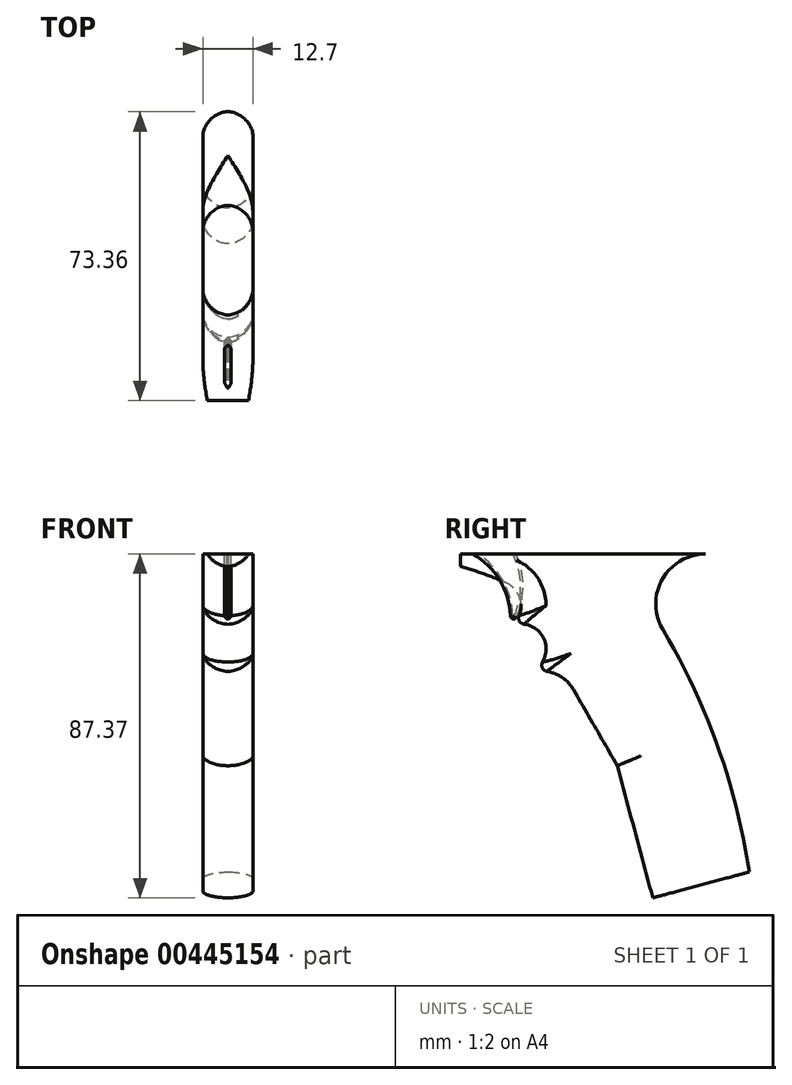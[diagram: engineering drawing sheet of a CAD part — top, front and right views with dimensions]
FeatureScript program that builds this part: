
annotation { "Feature Type Name" : "Feature", "Feature Type Description" : "" }
export const myFeature = defineFeature(function(context is Context, id is Id, definition is map)
    precondition{}
    {
        {
            var Q0;
            Q0=qCreatedBy(makeId("Right.planeOp"),FACE);
            var sketch = newSketch(context, id + "F0", { "sketchPlane" : qUnion([Q0])});
            skLineSegment(sketch, "E0", {"start": v(0, 0) * mm, "end": v(-76.2, 0) * mm});
            skLineSegment(sketch, "E1", {"start": v(-76.2, 0) * mm, "end": v(-76.2, -3.18) * mm});
            skLineSegment(sketch, "E2", {"start": v(-38.1, 0) * mm, "end": v(-12.7, -44) * mm});
            skLineSegment(sketch, "E3", {"start": v(-12.7, -44) * mm, "end": v(-2.84, -80.8) * mm});
            skLineSegment(sketch, "E4", {"start": v(-2.84, -80.8) * mm, "end": v(-27.37, -87.37) * mm});
            skLineSegment(sketch, "E5", {"start": v(-12.7, -44) * mm, "end": v(-36.37, -53.8) * mm});
            skLineSegment(sketch, "E6", {"start": v(-27.37, -87.37) * mm, "end": v(-36.37, -53.8) * mm});
            skLineSegment(sketch, "E7", {"start": v(-36.37, -53.8) * mm, "end": v(-67.43, 0) * mm});
            skArc(sketch, "E8", {"start": v(-2.84, -80.8) * mm, "mid": v(-10.85, -48.93) * mm, "end": v(-24.84, -19.19) * mm});
            skArc(sketch, "E9", {"start": v(-13.92, 0) * mm, "mid": v(-24.96, -6.42) * mm, "end": v(-24.84, -19.19) * mm});
            skArc(sketch, "E10", {"start": v(-64.57, -7.37) * mm, "mid": v(-70.3, -5.05) * mm, "end": v(-76.2, -3.17) * mm});
            skArc(sketch, "E11", {"start": v(-55.37, -27.43) * mm, "mid": v(-55.1, -21.37) * mm, "end": v(-60.05, -17.86) * mm});
            skArc(sketch, "E12", {"start": v(-61.32, -15.66) * mm, "mid": v(-61.25, -10.85) * mm, "end": v(-64.57, -7.37) * mm});
            skArc(sketch, "E13", {"start": v(-47.53, -34.46) * mm, "mid": v(-50.37, -31.38) * mm, "end": v(-54.26, -29.82) * mm});
            skArc(sketch, "E14", {"start": v(-55.37, -27.43) * mm, "mid": v(-55.45, -28.92) * mm, "end": v(-54.26, -29.82) * mm});
            skArc(sketch, "E15", {"start": v(-61.32, -15.66) * mm, "mid": v(-61.24, -17.08) * mm, "end": v(-60.05, -17.86) * mm});
            skPoint(sketch, "E16.orphan", {"position": v(-62.67, -8.25) * mm});
            skSolve(sketch);
        }
        {
            var Q0;
            {var subQ3=sQuery(id+"F0.wireOp",EDGE,"E2");Q0=makeQuery(id+"F0.imprint","IMPRINT",FACE,{"disambiguationData":[TD([[makeQuery(id+"F0.imprint","IMPRINT",EDGE,{"derivedFrom":subQ3}),-1.0]])]});}
            var Q1;
            {var subQ0=sQuery(id+"F0.wireOp",EDGE,"E2");Q1=makeQuery(id+"F0.imprint","IMPRINT",FACE,{"disambiguationData":[TD([[makeQuery(id+"F0.imprint","IMPRINT",EDGE,{"derivedFrom":subQ0}),1.0]])]});}
            var Q2;
            Q2=makeQuery(id+"F0.imprint","IMPRINT",FACE,{"disambiguationData":[TD([[makeQuery(id+"F0.imprint","IMPRINT",EDGE,{"derivedFrom":sQuery(id+"F0.wireOp",EDGE,"E3")}),-1.0]])]});
            var Q3;
            {var subQ0=sQuery(id+"F0.wireOp",EDGE,"E3");Q3=makeQuery(id+"F0.imprint","IMPRINT",FACE,{"disambiguationData":[TD([[makeQuery(id+"F0.imprint","IMPRINT",EDGE,{"derivedFrom":subQ0}),1.0]])]});}
            var Q4;
            {var subQ4=sQuery(id+"F0.wireOp",EDGE,"E6");Q4=makeQuery(id+"F0.imprint","IMPRINT",FACE,{"disambiguationData":[TD([[makeQuery(id+"F0.imprint","IMPRINT",EDGE,{"derivedFrom":subQ4}),1.0]])]});}
            var Q5;
            {var subQ5=sQuery(id+"F0.wireOp",EDGE,"E14");Q5=makeQuery(id+"F0.imprint","IMPRINT",FACE,{"disambiguationData":[TD([[makeQuery(id+"F0.imprint","IMPRINT",EDGE,{"derivedFrom":subQ5}),1.0]])]});}
            var Q6;
            {var subQ5=sQuery(id+"F0.wireOp",EDGE,"E15");Q6=makeQuery(id+"F0.imprint","IMPRINT",FACE,{"disambiguationData":[TD([[makeQuery(id+"F0.imprint","IMPRINT",EDGE,{"derivedFrom":subQ5}),1.0]])]});}
            var Q7;
            {var subQ1=sQuery(id+"F0.wireOp",EDGE,"E1");Q7=makeQuery(id+"F0.imprint","IMPRINT",FACE,{"disambiguationData":[TD([[makeQuery(id+"F0.imprint","IMPRINT",EDGE,{"derivedFrom":subQ1}),1.0]])]});}
            extrude(context, id + "F1", {"entities" : qUnion([Q0, Q1, Q2, Q3, Q4, Q5, Q6, Q7]), "endBound" : BoundingType.SYMMETRIC, "depth" : 12.7 * mm});
        }
        {
            var Q0;
            Q0=makeQuery(id+"F1.opExtrude","CAP_EDGE",EDGE,{"disambiguationData":[OSD([sQuery(id+"F0.wireOp",EDGE,"E13")])],"isStart":true});
            var Q1;
            Q1=makeQuery(id+"F1.opExtrude","CAP_EDGE",EDGE,{"disambiguationData":[OSD([sQuery(id+"F0.wireOp",EDGE,"E11")])],"isStart":false});
            var Q2;
            Q2=makeQuery(id+"F1.opExtrude","CAP_EDGE",EDGE,{"disambiguationData":[OSD([sQuery(id+"F0.wireOp",EDGE,"E7")])],"isStart":false});
            var Q3;
            Q3=makeQuery(id+"F1.opExtrude","CAP_EDGE",EDGE,{"disambiguationData":[OSD([sQuery(id+"F0.wireOp",EDGE,"E7")])],"isStart":true});
            var Q4;
            Q4=makeQuery(id+"F1.opExtrude","CAP_EDGE",EDGE,{"disambiguationData":[OSD([sQuery(id+"F0.wireOp",EDGE,"E6")])],"isStart":false});
            var Q5;
            Q5=makeQuery(id+"F1.opExtrude","CAP_EDGE",EDGE,{"disambiguationData":[OSD([sQuery(id+"F0.wireOp",EDGE,"E6")])],"isStart":true});
            var Q6;
            Q6=makeQuery(id+"F1.opExtrude","CAP_EDGE",EDGE,{"disambiguationData":[OSD([sQuery(id+"F0.wireOp",EDGE,"E8")])],"isStart":true});
            var Q7;
            Q7=makeQuery(id+"F1.opExtrude","CAP_EDGE",EDGE,{"disambiguationData":[OSD([sQuery(id+"F0.wireOp",EDGE,"E8")])],"isStart":false});
            fillet(context, id + "F2", {"entities" : qUnion([Q0, Q1, Q2, Q3, Q4, Q5, Q6, Q7]), "radius" : 6.35 * mm, "tangentPropagation" : true, "rho" : .375, "crossSection" : FilletCrossSection.CONIC, "allowEdgeOverflow" : false});
        }
        {
            var Q0;
            Q0=qCreatedBy(makeId("Right.planeOp"),FACE);
            var sketch = newSketch(context, id + "F3", { "sketchPlane" : qUnion([Q0])});
            skPoint(sketch, "E17.0", {"position": v(-76.2, 0) * mm});
            skLineSegment(sketch, "E18", {"start": v(-76.2, 0) * mm, "end": v(-73.03, 0) * mm});
            skArc(sketch, "E19", {"start": v(-63.51, -15.76) * mm, "mid": v(-66.24, -6.65) * mm, "end": v(-73.03, 0) * mm});
            skLineSegment(sketch, "E20", {"start": v(-76.2, 0) * mm, "end": v(-76.2, -16.5) * mm});
            skLineSegment(sketch, "E21", {"start": v(-76.2, -16.5) * mm, "end": v(-82.55, -16.5) * mm});
            skArc(sketch, "E22", {"start": v(-62, -16.05) * mm, "mid": v(-60.33, -8) * mm, "end": v(-62.2, 0) * mm});
            skLineSegment(sketch, "E23", {"start": v(-73.03, 0) * mm, "end": v(-62.2, 0) * mm});
            skArc(sketch, "E24", {"start": v(-63.51, -15.76) * mm, "mid": v(-62.87, -16.5) * mm, "end": v(-62, -16.05) * mm});
            skLineSegment(sketch, "E25", {"start": v(-79.38, -16.5) * mm, "end": v(-79.38, -8.25) * mm});
            skLineSegment(sketch, "E26", {"start": v(-76.2, -8.25) * mm, "end": v(-79.38, -8.25) * mm});
            skSolve(sketch);
        }
        {
            var Q0;
            Q0=makeQuery(id+"F3.imprint","IMPRINT",FACE,{"disambiguationData":[TD([[makeQuery(id+"F3.imprint","IMPRINT",EDGE,{"derivedFrom":sQuery(id+"F3.wireOp",EDGE,"E19")}),-1.0]])]});
            extrude(context, id + "F4", {"entities" : qUnion([Q0]), "endBound" : BoundingType.SYMMETRIC, "depth" : 1.59 * mm});
        }
        {
            var Q0;
            Q0=makeQuery(id+"F4.opExtrude","CAP_EDGE",EDGE,{"disambiguationData":[OSD([sQuery(id+"F3.wireOp",EDGE,"E19")])],"isStart":false});
            var Q1;
            Q1=makeQuery(id+"F4.opExtrude","CAP_EDGE",EDGE,{"disambiguationData":[OSD([sQuery(id+"F3.wireOp",EDGE,"E24")])],"isStart":false});
            var Q2;
            Q2=makeQuery(id+"F4.opExtrude","CAP_EDGE",EDGE,{"disambiguationData":[OSD([sQuery(id+"F3.wireOp",EDGE,"E22")])],"isStart":false});
            var Q3;
            Q3=makeQuery(id+"F4.opExtrude","CAP_EDGE",EDGE,{"disambiguationData":[OSD([sQuery(id+"F3.wireOp",EDGE,"E19")])],"isStart":true});
            chamfer(context, id + "F5", {"entities" : qUnion([Q0, Q1, Q2, Q3]), "width" : 0.64 * mm, "tangentPropagation" : true});
        }
    });
